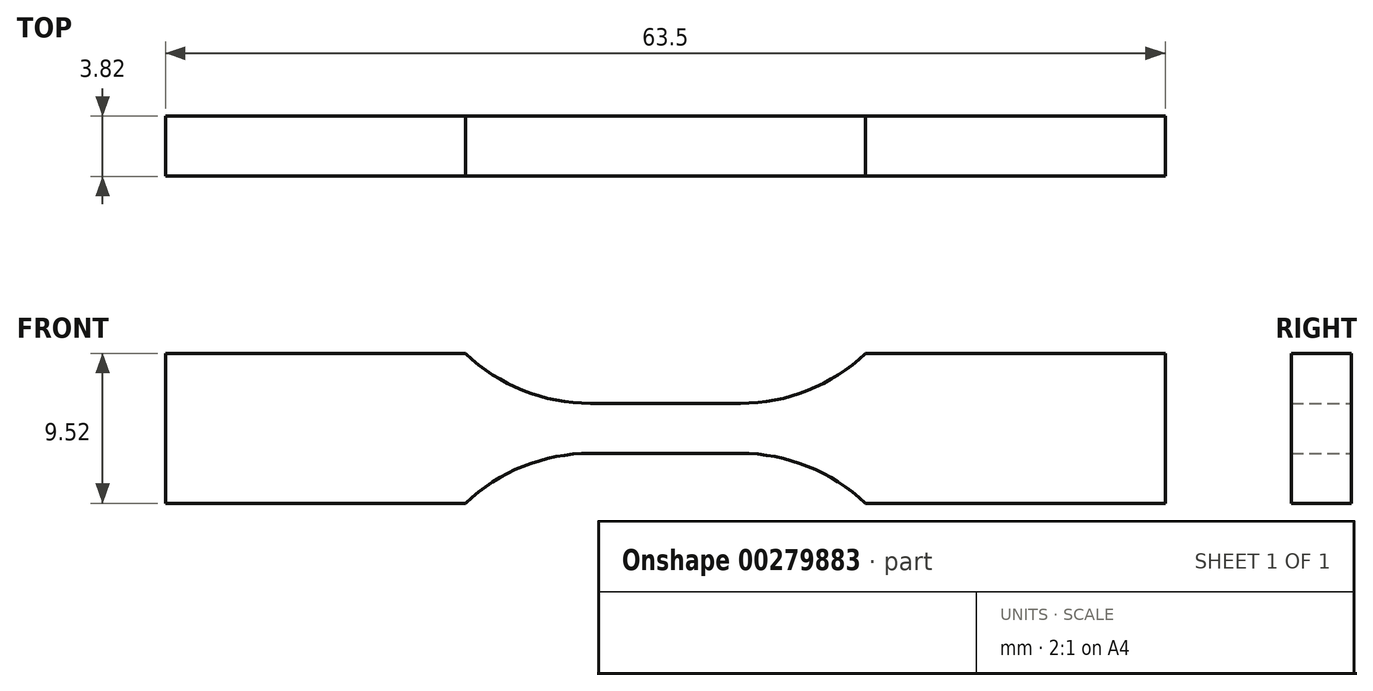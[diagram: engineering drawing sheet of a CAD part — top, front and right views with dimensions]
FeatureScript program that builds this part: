
annotation { "Feature Type Name" : "Feature", "Feature Type Description" : "" }
export const myFeature = defineFeature(function(context is Context, id is Id, definition is map)
    precondition{}
    {
        {
            var Q0;
            Q0=qCreatedBy(makeId("Front.planeOp"),FACE);
            var sketch = newSketch(context, id + "F0", { "sketchPlane" : qUnion([Q0])});
            skLineSegment(sketch, "E0", {"start": v(0, 1.59) * mm, "end": v(4.76, 1.59) * mm});
            skArc(sketch, "E1", {"start": v(4.76, 1.59) * mm, "mid": v(9.04, 2.41) * mm, "end": v(12.7, 4.76) * mm});
            skLineSegment(sketch, "E2", {"start": v(12.7, 4.76) * mm, "end": v(31.75, 4.76) * mm});
            skLineSegment(sketch, "E3.MirrorCS", {"start": v(12.7, -4.76) * mm, "end": v(31.75, -4.76) * mm});
            skLineSegment(sketch, "E4.MirrorCS", {"start": v(0, -1.59) * mm, "end": v(4.76, -1.59) * mm});
            skArc(sketch, "E5.MirrorCS", {"start": v(4.76, -1.59) * mm, "mid": v(9.04, -2.41) * mm, "end": v(12.7, -4.76) * mm});
            skArc(sketch, "E6.MirrorCS", {"start": v(-4.76, -1.59) * mm, "mid": v(-9.04, -2.41) * mm, "end": v(-12.7, -4.76) * mm});
            skLineSegment(sketch, "E7.MirrorCS", {"start": v(0, 1.59) * mm, "end": v(-4.76, 1.59) * mm});
            skArc(sketch, "E8.MirrorCS", {"start": v(-4.76, 1.59) * mm, "mid": v(-9.04, 2.41) * mm, "end": v(-12.7, 4.76) * mm});
            skLineSegment(sketch, "E9.MirrorCS", {"start": v(-12.7, -4.76) * mm, "end": v(-31.75, -4.76) * mm});
            skLineSegment(sketch, "E10.MirrorCS", {"start": v(0, -1.59) * mm, "end": v(-4.76, -1.59) * mm});
            skLineSegment(sketch, "E11.MirrorCS", {"start": v(-12.7, 4.76) * mm, "end": v(-31.75, 4.76) * mm});
            skLineSegment(sketch, "E12", {"start": v(31.75, 4.76) * mm, "end": v(31.75, -4.76) * mm});
            skLineSegment(sketch, "E13", {"start": v(-31.75, 4.76) * mm, "end": v(-31.75, -4.76) * mm});
            skSolve(sketch);
        }
        {
            var Q0;
            Q0=makeQuery(id+"F0.imprint","IMPRINT",FACE,{"disambiguationData":[TD([[makeQuery(id+"F0.imprint","IMPRINT",EDGE,{"derivedFrom":sQuery(id+"F0.wireOp",EDGE,"E0")}),-1.0]])]});
            extrude(context, id + "F1", {"entities" : qUnion([Q0]), "endBound" : BoundingType.SYMMETRIC, "depth" : 3.8 * mm});
        }
    });
